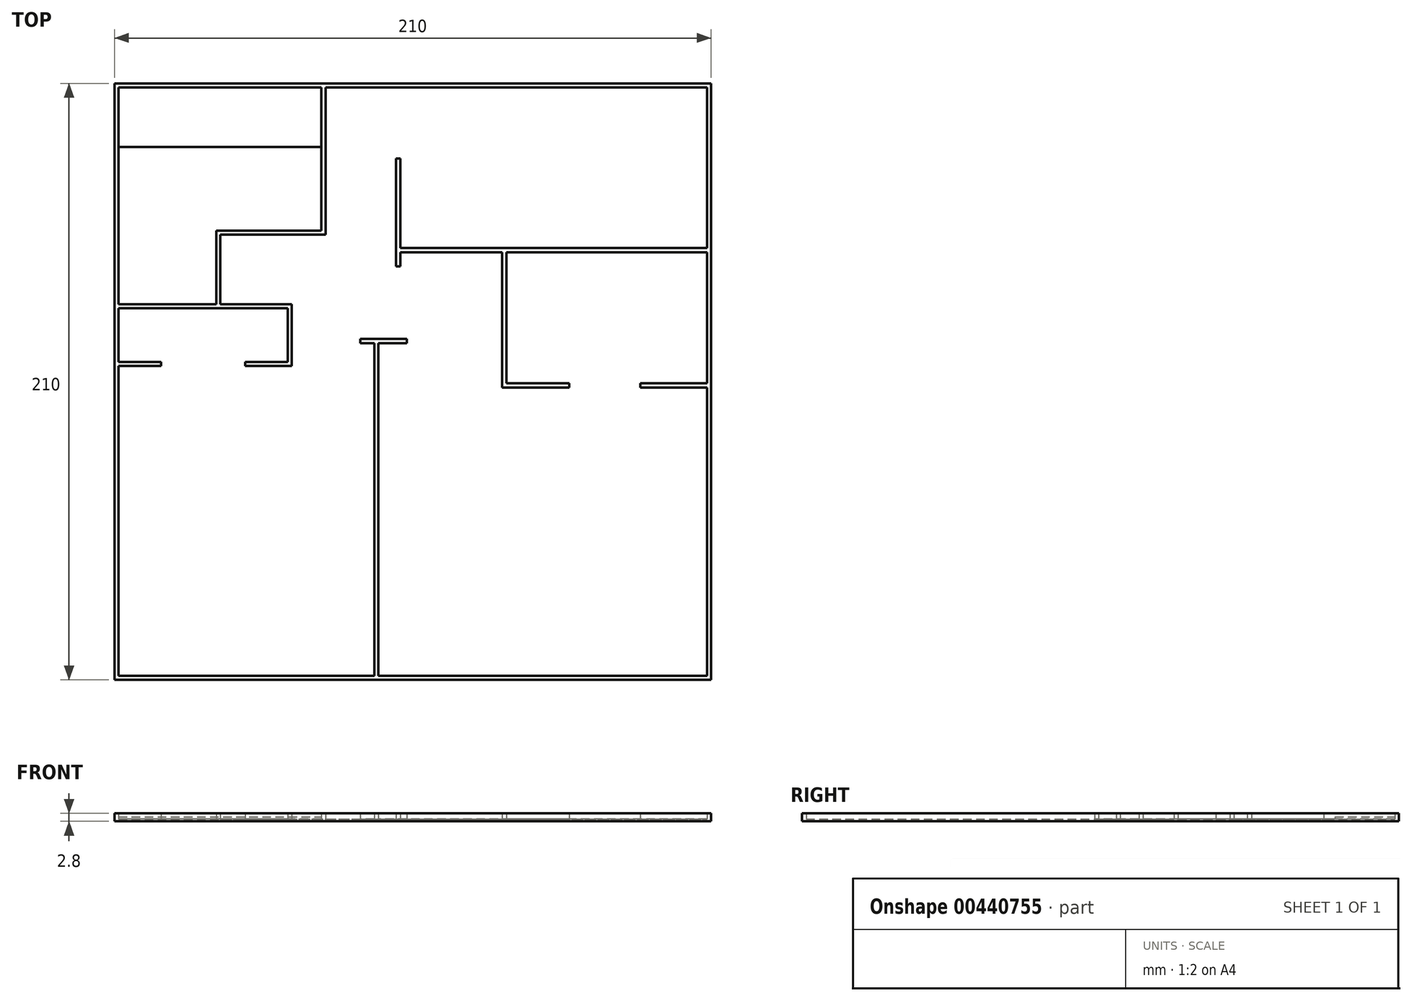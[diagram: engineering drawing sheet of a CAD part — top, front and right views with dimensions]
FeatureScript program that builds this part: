
annotation { "Feature Type Name" : "Feature", "Feature Type Description" : "" }
export const myFeature = defineFeature(function(context is Context, id is Id, definition is map)
    precondition{}
    {
        {
            var Q0;
            Q0=qCreatedBy(makeId("Top.planeOp"),FACE);
            var sketch = newSketch(context, id + "F0", { "sketchPlane" : qUnion([Q0])});
            skLineSegment(sketch, "E0.bottom", {"start": v(0, 0) * mm, "end": v(210, 0) * mm});
            skLineSegment(sketch, "E0.top", {"start": v(0, 210) * mm, "end": v(210, 210) * mm});
            skLineSegment(sketch, "E0.left", {"start": v(0, 0) * mm, "end": v(0, 210) * mm});
            skLineSegment(sketch, "E0.right", {"start": v(210, 0) * mm, "end": v(210, 210) * mm});
            skSolve(sketch);
        }
        {
            var Q0;
            Q0=makeQuery(id+"F0.imprint","IMPRINT",FACE,{"disambiguationData":[TD([[makeQuery(id+"F0.imprint","IMPRINT",EDGE,{"derivedFrom":sQuery(id+"F0.wireOp",EDGE,"E0.bottom")}),1.0]])]});
            extrude(context, id + "F1", {"entities" : qUnion([Q0]), "depth" : .8 * mm});
        }
        {
            var Q0;
            Q0=makeQuery(id+"F1.opExtrude","CAP_FACE",FACE,{"disambiguationData":[OSD([sQuery(id+"F0.wireOp",EDGE,"E0.bottom"),sQuery(id+"F0.wireOp",EDGE,"E0.top"),sQuery(id+"F0.wireOp",EDGE,"E0.left"),sQuery(id+"F0.wireOp",EDGE,"E0.right")])],"isStart":false});
            var sketch = newSketch(context, id + "F2", { "sketchPlane" : qUnion([Q0])});
            skLineSegment(sketch, "E1.0", {"start": v(1.44, 1.44) * mm, "end": v(208.56, 1.44) * mm});
            skLineSegment(sketch, "E1.1", {"start": v(1.44, 1.44) * mm, "end": v(1.44, 208.56) * mm});
            skLineSegment(sketch, "E1.2", {"start": v(1.44, 208.56) * mm, "end": v(208.56, 208.56) * mm});
            skLineSegment(sketch, "E1.3", {"start": v(208.56, 1.44) * mm, "end": v(208.56, 208.56) * mm});
            skLineSegment(sketch, "E2.0", {"start": v(0, 0) * mm, "end": v(210, 0) * mm});
            skLineSegment(sketch, "E3.0", {"start": v(0, 0) * mm, "end": v(0, 210) * mm});
            skLineSegment(sketch, "E4.0", {"start": v(0, 210) * mm, "end": v(210, 210) * mm});
            skLineSegment(sketch, "E5.0", {"start": v(210, 0) * mm, "end": v(210, 210) * mm});
            skSolve(sketch);
        }
        {
            var Q0;
            Q0=qSketchRegion(id+"F2",true);
            extrude(context, id + "F3", {"entities" : qUnion([Q0]), "operationType" : NewBodyOperationType.ADD, "depth" : 2 * mm});
        }
        {
            var Q0;
            Q0=makeQuery(id+"F1.opExtrude","CAP_FACE",FACE,{"disambiguationData":[OSD([sQuery(id+"F0.wireOp",EDGE,"E0.bottom"),sQuery(id+"F0.wireOp",EDGE,"E0.top"),sQuery(id+"F0.wireOp",EDGE,"E0.left"),sQuery(id+"F0.wireOp",EDGE,"E0.right")])],"isStart":false});
            var sketch = newSketch(context, id + "F4", { "sketchPlane" : qUnion([Q0])});
            skLineSegment(sketch, "E6", {"start": v(74.28, 208.56) * mm, "end": v(74.28, 156.72) * mm});
            skLineSegment(sketch, "E7", {"start": v(35.77, 158.16) * mm, "end": v(35.77, 132.3) * mm});
            skLineSegment(sketch, "E8", {"start": v(35.77, 130.86) * mm, "end": v(60.97, 130.86) * mm});
            skLineSegment(sketch, "E9", {"start": v(62.4, 132.3) * mm, "end": v(37.2, 132.3) * mm});
            skLineSegment(sketch, "E10", {"start": v(37.2, 132.3) * mm, "end": v(37.2, 156.72) * mm});
            skLineSegment(sketch, "E11", {"start": v(37.2, 156.72) * mm, "end": v(74.28, 156.72) * mm});
            skLineSegment(sketch, "E12", {"start": v(72.84, 208.56) * mm, "end": v(74.28, 208.56) * mm});
            skLineSegment(sketch, "E13", {"start": v(72.84, 208.56) * mm, "end": v(72.84, 158.16) * mm});
            skLineSegment(sketch, "E14.trimOffspring", {"start": v(72.84, 158.16) * mm, "end": v(35.77, 158.16) * mm});
            skLineSegment(sketch, "E15", {"start": v(62.4, 132.3) * mm, "end": v(62.4, 130.86) * mm});
            skLineSegment(sketch, "E16", {"start": v(35.77, 132.3) * mm, "end": v(1.44, 132.3) * mm});
            skLineSegment(sketch, "E17", {"start": v(35.77, 130.86) * mm, "end": v(1.44, 130.86) * mm});
            skLineSegment(sketch, "E18", {"start": v(1.44, 130.86) * mm, "end": v(1.44, 132.3) * mm});
            skLineSegment(sketch, "E19", {"start": v(62.4, 130.86) * mm, "end": v(62.4, 110.52) * mm});
            skLineSegment(sketch, "E20", {"start": v(62.4, 110.52) * mm, "end": v(45.97, 110.52) * mm});
            skLineSegment(sketch, "E21", {"start": v(45.97, 110.52) * mm, "end": v(45.97, 111.96) * mm});
            skLineSegment(sketch, "E22", {"start": v(45.97, 111.96) * mm, "end": v(60.97, 111.96) * mm});
            skLineSegment(sketch, "E23", {"start": v(60.97, 111.96) * mm, "end": v(60.97, 130.86) * mm});
            skLineSegment(sketch, "E24.bottom", {"start": v(1.44, 110.52) * mm, "end": v(16.44, 110.52) * mm});
            skLineSegment(sketch, "E24.top", {"start": v(1.44, 111.96) * mm, "end": v(16.44, 111.96) * mm});
            skLineSegment(sketch, "E24.left", {"start": v(1.44, 110.52) * mm, "end": v(1.44, 111.96) * mm});
            skLineSegment(sketch, "E24.right", {"start": v(16.44, 110.52) * mm, "end": v(16.44, 111.96) * mm});
            skLineSegment(sketch, "E25", {"start": v(208.56, 152.02) * mm, "end": v(100.56, 152.02) * mm});
            skLineSegment(sketch, "E26", {"start": v(100.56, 152.02) * mm, "end": v(100.56, 183.56) * mm});
            skLineSegment(sketch, "E27", {"start": v(100.56, 183.56) * mm, "end": v(99.12, 183.56) * mm});
            skLineSegment(sketch, "E28", {"start": v(99.12, 183.56) * mm, "end": v(99.12, 145.58) * mm});
            skLineSegment(sketch, "E29", {"start": v(99.12, 145.58) * mm, "end": v(100.56, 145.58) * mm});
            skLineSegment(sketch, "E30", {"start": v(100.56, 145.58) * mm, "end": v(100.56, 150.58) * mm});
            skLineSegment(sketch, "E31", {"start": v(100.56, 150.58) * mm, "end": v(136.45, 150.58) * mm});
            skLineSegment(sketch, "E32", {"start": v(136.45, 150.58) * mm, "end": v(136.45, 102.94) * mm});
            skLineSegment(sketch, "E33", {"start": v(136.45, 102.94) * mm, "end": v(160, 102.94) * mm});
            skLineSegment(sketch, "E34", {"start": v(160, 102.94) * mm, "end": v(160, 104.38) * mm});
            skLineSegment(sketch, "E35", {"start": v(160, 104.38) * mm, "end": v(137.89, 104.38) * mm});
            skLineSegment(sketch, "E36", {"start": v(137.89, 104.38) * mm, "end": v(137.89, 150.58) * mm});
            skLineSegment(sketch, "E37", {"start": v(137.89, 150.58) * mm, "end": v(208.56, 150.58) * mm});
            skLineSegment(sketch, "E38", {"start": v(208.56, 150.58) * mm, "end": v(208.56, 152.02) * mm});
            skLineSegment(sketch, "E39.bottom", {"start": v(185, 104.38) * mm, "end": v(208.56, 104.38) * mm});
            skLineSegment(sketch, "E39.top", {"start": v(185, 102.94) * mm, "end": v(208.56, 102.94) * mm});
            skLineSegment(sketch, "E39.left", {"start": v(185, 104.38) * mm, "end": v(185, 102.94) * mm});
            skLineSegment(sketch, "E39.right", {"start": v(208.56, 104.38) * mm, "end": v(208.56, 102.94) * mm});
            skLineSegment(sketch, "E40", {"start": v(92.88, 1.44) * mm, "end": v(91.44, 1.44) * mm});
            skLineSegment(sketch, "E41", {"start": v(91.44, 1.44) * mm, "end": v(91.44, 118.56) * mm});
            skLineSegment(sketch, "E42", {"start": v(91.44, 118.56) * mm, "end": v(86.44, 118.56) * mm});
            skLineSegment(sketch, "E43", {"start": v(86.44, 118.56) * mm, "end": v(86.44, 120) * mm});
            skLineSegment(sketch, "E44", {"start": v(86.44, 120) * mm, "end": v(102.88, 120) * mm});
            skLineSegment(sketch, "E45", {"start": v(102.88, 120) * mm, "end": v(102.88, 118.56) * mm});
            skLineSegment(sketch, "E46", {"start": v(102.88, 118.56) * mm, "end": v(92.88, 118.56) * mm});
            skLineSegment(sketch, "E47", {"start": v(92.88, 118.56) * mm, "end": v(92.88, 1.44) * mm});
            skSolve(sketch);
        }
        {
            var Q0;
            Q0=qSketchRegion(id+"F4",true);
            var Q1;
            Q1=makeQuery(id+"F3.opExtrude","CAP_FACE",FACE,{"disambiguationData":[OSD([sQuery(id+"F2.wireOp",EDGE,"E1.0"),sQuery(id+"F2.wireOp",EDGE,"E1.1"),sQuery(id+"F2.wireOp",EDGE,"E1.2"),sQuery(id+"F2.wireOp",EDGE,"E1.3"),sQuery(id+"F2.wireOp",EDGE,"E2.0"),sQuery(id+"F2.wireOp",EDGE,"E3.0"),sQuery(id+"F2.wireOp",EDGE,"E4.0"),sQuery(id+"F2.wireOp",EDGE,"E5.0")])],"isStart":false});
            extrude(context, id + "F5", {"entities" : qUnion([Q0]), "operationType" : NewBodyOperationType.ADD, "endBound" : BoundingType.UP_TO_SURFACE, "endBoundEntityFace" : qUnion([Q1]), "depth" : 25 * mm});
        }
        {
            var Q0;
            Q0=makeQuery(id+"F1.opExtrude","CAP_FACE",FACE,{"disambiguationData":[OSD([sQuery(id+"F0.wireOp",EDGE,"E0.bottom"),sQuery(id+"F0.wireOp",EDGE,"E0.top"),sQuery(id+"F0.wireOp",EDGE,"E0.left"),sQuery(id+"F0.wireOp",EDGE,"E0.right")])],"isStart":false});
            var sketch = newSketch(context, id + "F6", { "sketchPlane" : qUnion([Q0])});
            skLineSegment(sketch, "E48.bottom", {"start": v(1.44, 208.56) * mm, "end": v(72.84, 208.56) * mm});
            skLineSegment(sketch, "E48.top", {"start": v(1.44, 187.56) * mm, "end": v(72.84, 187.56) * mm});
            skLineSegment(sketch, "E48.left", {"start": v(1.44, 208.56) * mm, "end": v(1.44, 187.56) * mm});
            skLineSegment(sketch, "E48.right", {"start": v(72.84, 208.56) * mm, "end": v(72.84, 187.56) * mm});
            skSolve(sketch);
        }
        {
            var Q0;
            Q0=qSketchRegion(id+"F6",true);
            extrude(context, id + "F7", {"entities" : qUnion([Q0]), "operationType" : NewBodyOperationType.ADD, "depth" : .8 * mm});
        }
    });
